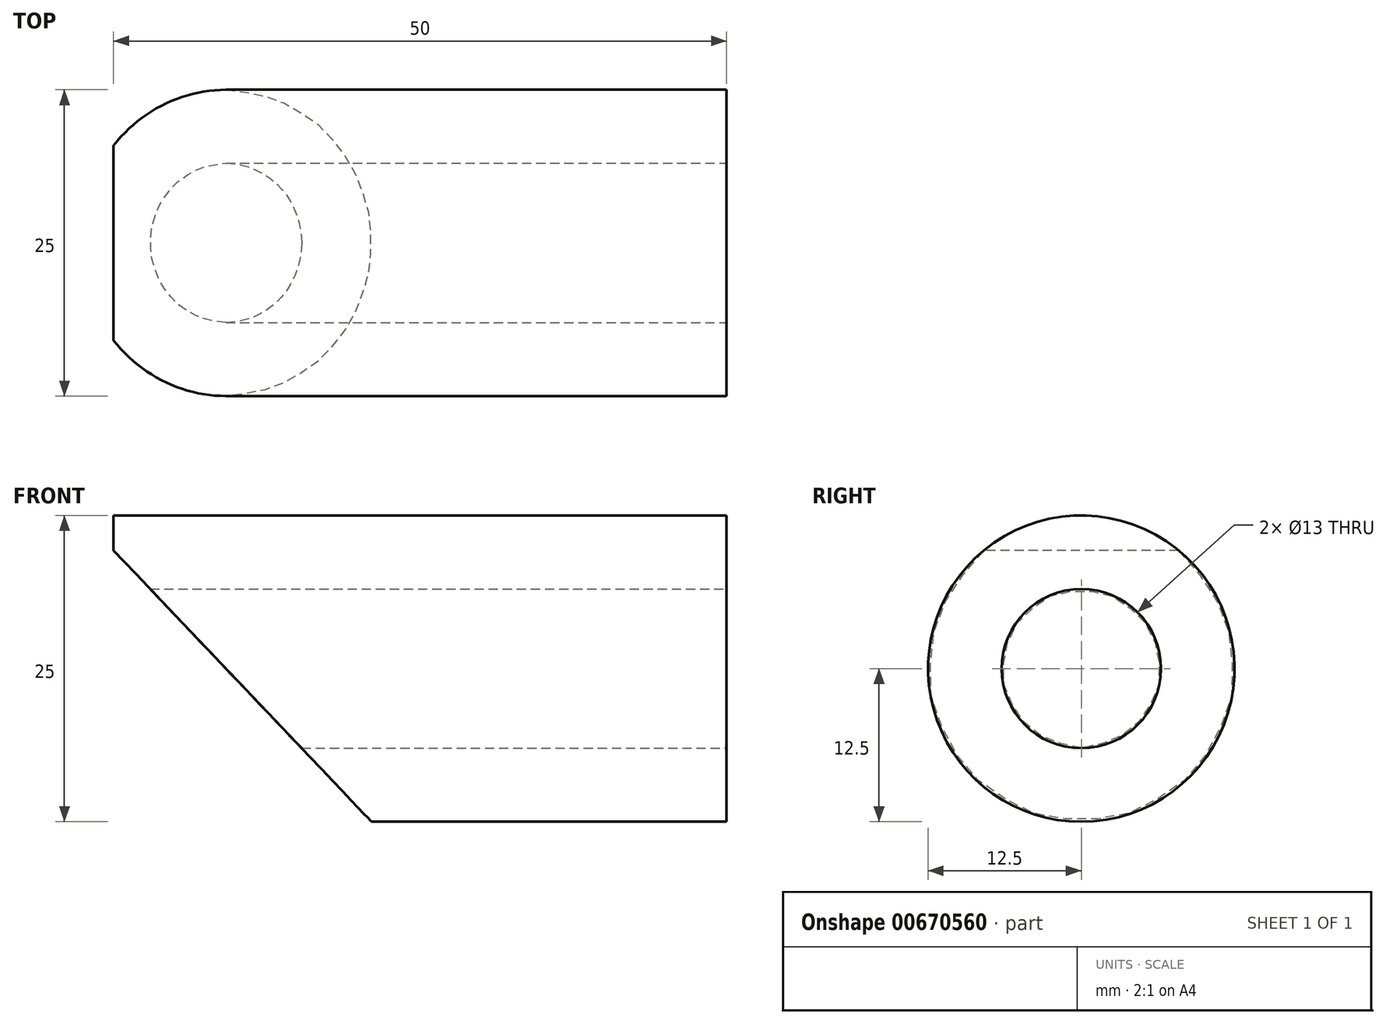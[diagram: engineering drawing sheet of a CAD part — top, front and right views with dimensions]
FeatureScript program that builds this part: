
annotation { "Feature Type Name" : "Feature", "Feature Type Description" : "" }
export const myFeature = defineFeature(function(context is Context, id is Id, definition is map)
    precondition{}
    {
        {
            var Q0;
            Q0=qCreatedBy(makeId("Right.planeOp"),FACE);
            var sketch = newSketch(context, id + "F0", { "sketchPlane" : qUnion([Q0])});
            skCircle(sketch, "E0", {"center": v(0, 0) * mm, "radius": 12.5 * mm});
            skSolve(sketch);
        }
        {
            var Q0;
            Q0=makeQuery(id+"F0.imprint","IMPRINT",FACE,{"disambiguationData":[TD([[makeQuery(id+"F0.imprint","IMPRINT",EDGE,{"derivedFrom":sQuery(id+"F0.wireOp",EDGE,"E0")}),1.0]])]});
            extrude(context, id + "F1", {"entities" : qUnion([Q0]), "depth" : 50 * mm, "offsetDistance" : 25 * mm});
        }
        {
            var Q0;
            Q0=makeQuery(id+"F1.opExtrude","CAP_FACE",FACE,{"disambiguationData":[OSD([sQuery(id+"F0.wireOp",EDGE,"E0")])],"isStart":false});
            var sketch = newSketch(context, id + "F2", { "sketchPlane" : qUnion([Q0])});
            skCircle(sketch, "E1", {"center": v(0, 0) * mm, "radius": 6.5 * mm});
            skSolve(sketch);
        }
        {
            var Q0;
            Q0=makeQuery(id+"F2.imprint","IMPRINT",FACE,{"disambiguationData":[TD([[makeQuery(id+"F2.imprint","IMPRINT",EDGE,{"derivedFrom":sQuery(id+"F2.wireOp",EDGE,"E1")}),1.0]])]});
            var Q1;
            Q1=makeQuery(id+"F1.opExtrude","CAP_FACE",FACE,{"disambiguationData":[OSD([sQuery(id+"F0.wireOp",EDGE,"E0")])],"isStart":true});
            extrude(context, id + "F3", {"entities" : qUnion([Q0]), "operationType" : NewBodyOperationType.REMOVE, "endBound" : BoundingType.UP_TO_SURFACE, "oppositeDirection" : true, "depth" : 25 * mm, "endBoundEntityFace" : qUnion([Q1]), "offsetDistance" : 25 * mm});
        }
        {
            var Q0;
            Q0=qCreatedBy(makeId("Front.planeOp"),FACE);
            var sketch = newSketch(context, id + "F4", { "sketchPlane" : qUnion([Q0])});
            skLineSegment(sketch, "E2", {"start": v(0, 12.5) * mm, "end": v(50, 12.5) * mm});
            skLineSegment(sketch, "E3", {"start": v(50, -12.5) * mm, "end": v(0, -12.5) * mm});
            skLineSegment(sketch, "E4", {"start": v(0, 9.65) * mm, "end": v(21.05, -12.5) * mm});
            skLineSegment(sketch, "E5", {"start": v(21.05, -12.5) * mm, "end": v(0, -12.5) * mm});
            skLineSegment(sketch, "E6", {"start": v(0, 9.65) * mm, "end": v(0, -12.5) * mm});
            skLineSegment(sketch, "E7", {"start": v(0, -12.5) * mm, "end": v(21.05, -12.5) * mm});
            skSolve(sketch);
        }
        {
            var Q0;
            Q0=qSketchRegion(id+"F4",true);
            extrude(context, id + "F5", {"entities" : qUnion([Q0]), "operationType" : NewBodyOperationType.REMOVE, "endBound" : BoundingType.THROUGH_ALL, "oppositeDirection" : true, "depth" : 25 * mm, "offsetDistance" : 25 * mm, "hasSecondDirection" : true, "secondDirectionBound" : SecondDirectionBoundingType.THROUGH_ALL, "secondDirectionOppositeDirection" : false, "secondDirectionDepth" : 25 * mm});
        }
    });
